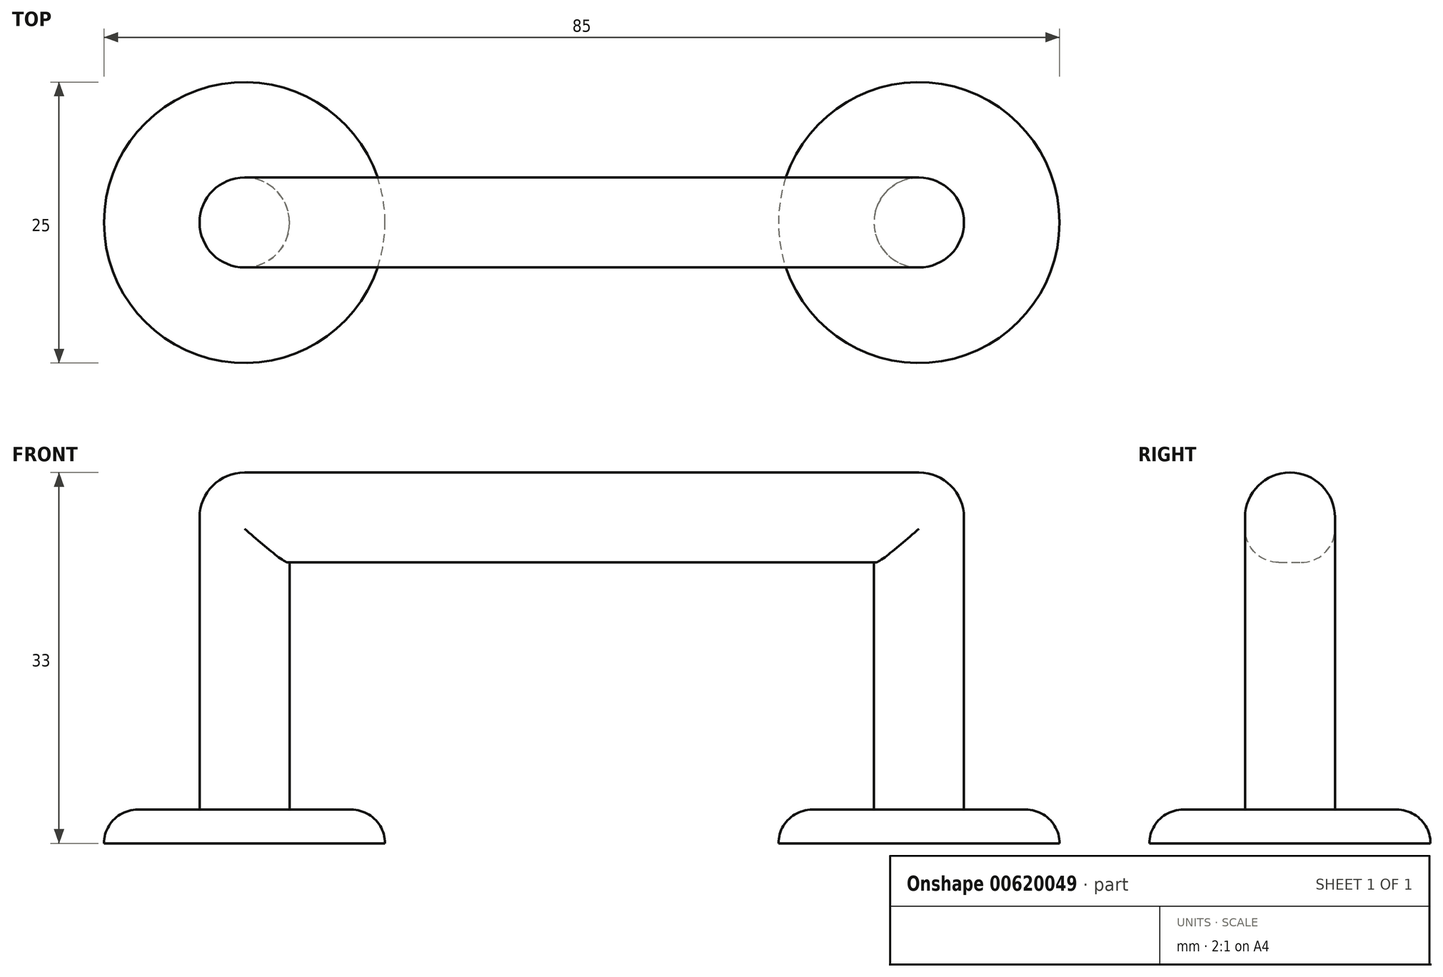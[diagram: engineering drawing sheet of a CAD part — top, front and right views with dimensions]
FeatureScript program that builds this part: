
annotation { "Feature Type Name" : "Feature", "Feature Type Description" : "" }
export const myFeature = defineFeature(function(context is Context, id is Id, definition is map)
    precondition{}
    {
        {
            var Q0;
            Q0=qCreatedBy(makeId("Top.planeOp"),FACE);
            var sketch = newSketch(context, id + "F0", { "sketchPlane" : qUnion([Q0])});
            skCircle(sketch, "E0", {"center": v(-30, 0) * mm, "radius": 12.5 * mm});
            skCircle(sketch, "E1", {"center": v(30, 0) * mm, "radius": 12.5 * mm});
            skSolve(sketch);
        }
        {
            var Q0;
            Q0 = qSketchRegion(id + "F0", true);
            extrude(context, id + "F1", {"entities" : qUnion([Q0]), "depth" : 3 * mm, "offsetDistance" : 25 * mm});
        }
        {
            var Q0;
            Q0=makeQuery(id+"F1.opExtrude","CAP_FACE",FACE,{"disambiguationData":[OSD([sQuery(id+"F0.wireOp",EDGE,"E0")])],"isStart":false});
            var sketch = newSketch(context, id + "F2", { "sketchPlane" : qUnion([Q0])});
            skCircle(sketch, "E2", {"center": v(-30, 0) * mm, "radius": 4 * mm});
            skCircle(sketch, "E3", {"center": v(30, 0) * mm, "radius": 4 * mm});
            skSolve(sketch);
        }
        {
            var Q0;
            Q0 = qSketchRegion(id + "F2", true);
            extrude(context, id + "F3", {"entities" : qUnion([Q0]), "operationType" : NewBodyOperationType.ADD, "depth" : 30 * mm, "offsetDistance" : 25 * mm});
        }
        {
            var Q0;
            Q0=makeQuery(id+"F3.opExtrude","CAP_FACE",FACE,{"disambiguationData":[OSD([sQuery(id+"F2.wireOp",EDGE,"E3")])],"isStart":false});
            var sketch = newSketch(context, id + "F4", { "sketchPlane" : qUnion([Q0])});
            skLineSegment(sketch, "E4", {"start": v(-34, 4) * mm, "end": v(34, 4) * mm});
            skLineSegment(sketch, "E5", {"start": v(34, 4) * mm, "end": v(34, -4) * mm});
            skLineSegment(sketch, "E6", {"start": v(34, -4) * mm, "end": v(-34, -4) * mm});
            skLineSegment(sketch, "E7", {"start": v(-34, -4) * mm, "end": v(-34, 4) * mm});
            skSolve(sketch);
        }
        {
            var Q0;
            Q0 = qSketchRegion(id + "F4", true);
            extrude(context, id + "F5", {"entities" : qUnion([Q0]), "operationType" : NewBodyOperationType.ADD, "oppositeDirection" : true, "depth" : 8 * mm, "offsetDistance" : 25 * mm});
        }
        {
            var Q0;
            Q0=makeQuery(id+"F5.opExtrude","CAP_EDGE",EDGE,{"disambiguationData":[OSD([sQuery(id+"F4.wireOp",EDGE,"E5")])],"isStart":true});
            var Q1;
            Q1=makeQuery(id+"F5.opExtrude","CAP_EDGE",EDGE,{"disambiguationData":[OSD([sQuery(id+"F4.wireOp",EDGE,"E4")])],"isStart":true});
            var Q2;
            Q2=makeQuery(id+"F5.opExtrude","CAP_EDGE",EDGE,{"disambiguationData":[OSD([sQuery(id+"F4.wireOp",EDGE,"E7")])],"isStart":true});
            var Q3;
            Q3=makeQuery(id+"F5.opExtrude","CAP_EDGE",EDGE,{"disambiguationData":[OSD([sQuery(id+"F4.wireOp",EDGE,"E6")])],"isStart":true});
            var Q4;
            Q4=makeQuery(id+"F5.opExtrude","SWEPT_EDGE",EDGE,{"disambiguationData":[OSD([sQuery(id+"F4.wireOp",EDGE,"E5"),sQuery(id+"F4.wireOp",EDGE,"E6")])]});
            var Q5;
            Q5=makeQuery(id+"F5.opExtrude","SWEPT_EDGE",EDGE,{"disambiguationData":[OSD([sQuery(id+"F4.wireOp",EDGE,"E4"),sQuery(id+"F4.wireOp",EDGE,"E5")])]});
            var Q6;
            Q6=makeQuery(id+"F5.opExtrude","SWEPT_EDGE",EDGE,{"disambiguationData":[OSD([sQuery(id+"F4.wireOp",EDGE,"E6"),sQuery(id+"F4.wireOp",EDGE,"E7")])]});
            var Q7;
            Q7=makeQuery(id+"F5.opExtrude","SWEPT_EDGE",EDGE,{"disambiguationData":[OSD([sQuery(id+"F4.wireOp",EDGE,"E4"),sQuery(id+"F4.wireOp",EDGE,"E7")])]});
            fillet(context, id + "F6", {"entities" : qUnion([Q0, Q1, Q2, Q3, Q4, Q5, Q6, Q7]), "radius" : 4 * mm, "tangentPropagation" : true, "allowEdgeOverflow" : false});
        }
        {
            var Q0;
            {var subQ0=sQuery(id+"F4.wireOp",EDGE,"E6");Q0=makeQuery(id+"F5.boolean.opBoolean","SPLIT",EDGE,{"disambiguationData":[TD([makeQuery(id+"F3.opExtrude","SWEPT_FACE",FACE,{"disambiguationData":[OSD([sQuery(id+"F2.wireOp",EDGE,"E2")])]}),makeQuery(id+"F3.opExtrude","SWEPT_FACE",FACE,{"disambiguationData":[OSD([sQuery(id+"F2.wireOp",EDGE,"E3")])]}),makeQuery(id+"F5.opExtrude","CAP_FACE",FACE,{"disambiguationData":[OSD([sQuery(id+"F4.wireOp",EDGE,"E4"),sQuery(id+"F4.wireOp",EDGE,"E5"),subQ0,sQuery(id+"F4.wireOp",EDGE,"E7")])],"isStart":false}),makeQuery(id+"F5.opExtrude","SWEPT_FACE",FACE,{"disambiguationData":[OSD([subQ0])]})])],"derivedFrom":makeQuery(id+"F5.opExtrude","CAP_EDGE",EDGE,{"disambiguationData":[OSD([subQ0])],"isStart":false})});}
            var Q1;
            {var subQ0=sQuery(id+"F4.wireOp",EDGE,"E4");Q1=makeQuery(id+"F5.boolean.opBoolean","SPLIT",EDGE,{"disambiguationData":[TD([makeQuery(id+"F3.opExtrude","SWEPT_FACE",FACE,{"disambiguationData":[OSD([sQuery(id+"F2.wireOp",EDGE,"E2")])]}),makeQuery(id+"F3.opExtrude","SWEPT_FACE",FACE,{"disambiguationData":[OSD([sQuery(id+"F2.wireOp",EDGE,"E3")])]}),makeQuery(id+"F5.opExtrude","SWEPT_FACE",FACE,{"disambiguationData":[OSD([subQ0])]}),makeQuery(id+"F5.opExtrude","CAP_FACE",FACE,{"disambiguationData":[OSD([subQ0,sQuery(id+"F4.wireOp",EDGE,"E5"),sQuery(id+"F4.wireOp",EDGE,"E6"),sQuery(id+"F4.wireOp",EDGE,"E7")])],"isStart":false})])],"derivedFrom":makeQuery(id+"F5.opExtrude","CAP_EDGE",EDGE,{"disambiguationData":[OSD([subQ0])],"isStart":false})});}
            fillet(context, id + "F7", {"entities" : qUnion([Q0, Q1]), "radius" : 3 * mm, "tangentPropagation" : true, "allowEdgeOverflow" : false});
        }
        {
            var Q0;
            Q0=makeQuery(id+"F3.opExtrude","CAP_EDGE",EDGE,{"disambiguationData":[OSD([sQuery(id+"F2.wireOp",EDGE,"E2")])],"isStart":true});
            var Q1;
            Q1=makeQuery(id+"F3.opExtrude","CAP_EDGE",EDGE,{"disambiguationData":[OSD([sQuery(id+"F2.wireOp",EDGE,"E3")])],"isStart":true});
            var Q2;
            Q2=makeQuery(id+"F1.opExtrude","CAP_EDGE",EDGE,{"disambiguationData":[OSD([sQuery(id+"F0.wireOp",EDGE,"E1")])],"isStart":false});
            var Q3;
            Q3=makeQuery(id+"F1.opExtrude","CAP_EDGE",EDGE,{"disambiguationData":[OSD([sQuery(id+"F0.wireOp",EDGE,"E0")])],"isStart":false});
            fillet(context, id + "F8", {"entities" : qUnion([Q0, Q1, Q2, Q3]), "radius" : 3 * mm, "tangentPropagation" : true, "allowEdgeOverflow" : false});
        }
    });
